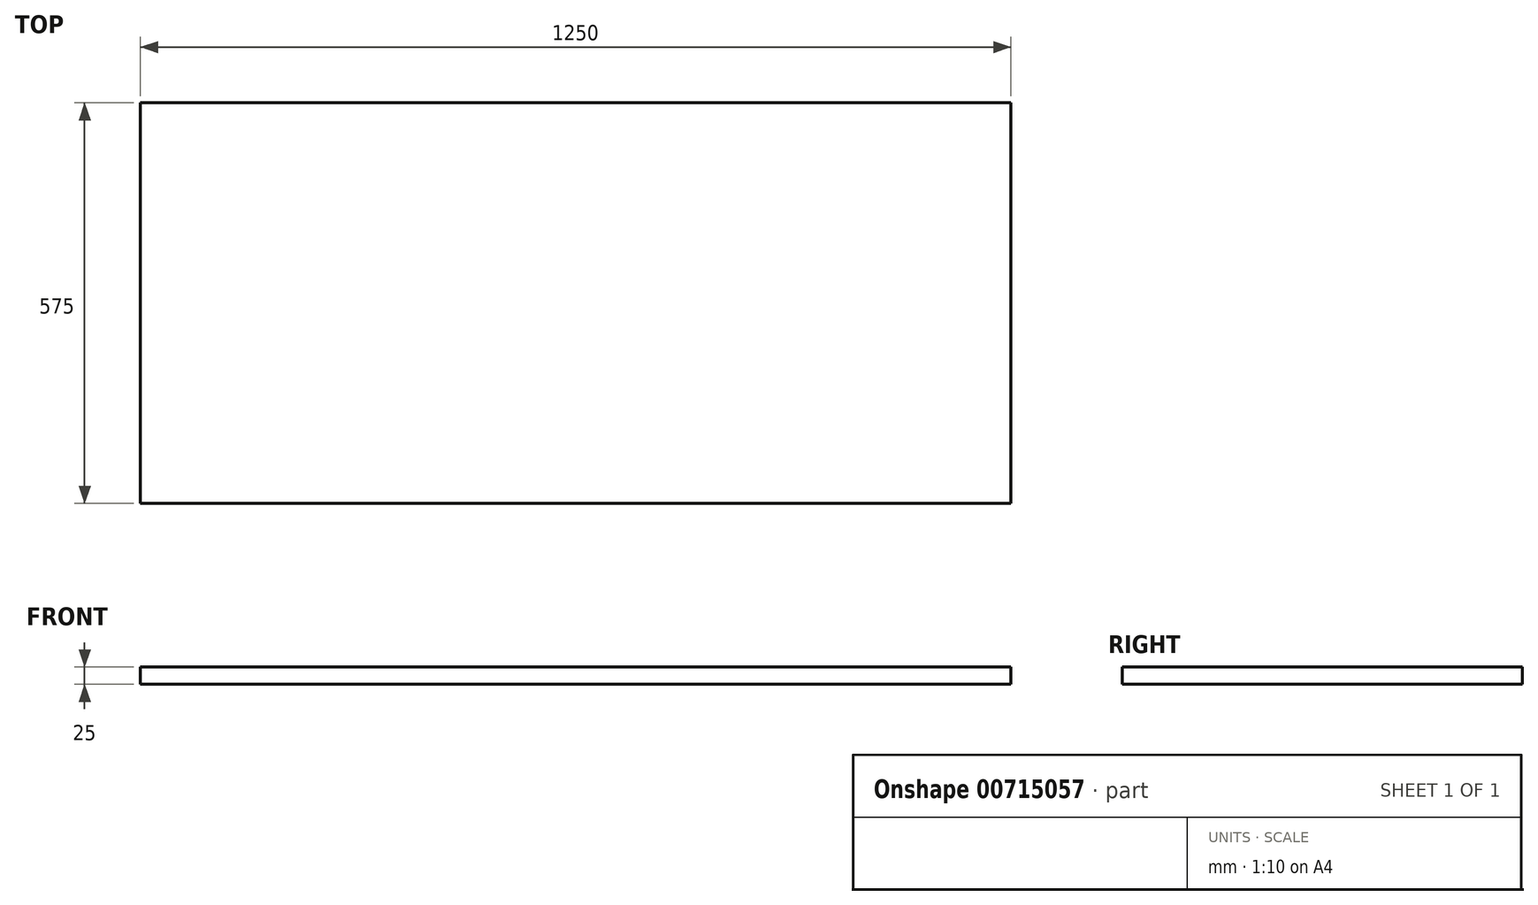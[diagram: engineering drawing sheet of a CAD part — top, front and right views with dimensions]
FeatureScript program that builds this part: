
annotation { "Feature Type Name" : "Feature", "Feature Type Description" : "" }
export const myFeature = defineFeature(function(context is Context, id is Id, definition is map)
    precondition{}
    {
        {
            var Q0;
            Q0=qCreatedBy(makeId("Top.planeOp"),FACE);
            var sketch = newSketch(context, id + "F0", { "sketchPlane" : qUnion([Q0])});
            skLineSegment(sketch, "E0.bottom", {"start": v(625, 287.5) * mm, "end": v(-625, 287.5) * mm});
            skLineSegment(sketch, "E0.top", {"start": v(625, -287.5) * mm, "end": v(-625, -287.5) * mm});
            skLineSegment(sketch, "E0.left", {"start": v(625, 287.5) * mm, "end": v(625, -287.5) * mm});
            skLineSegment(sketch, "E0.right", {"start": v(-625, 287.5) * mm, "end": v(-625, -287.5) * mm});
            skPoint(sketch, "E0.middle", {"position": v(0, 0) * mm});
            skSolve(sketch);
        }
        {
            var Q0;
            Q0=makeQuery(id+"F0.imprint","IMPRINT",FACE,{"disambiguationData":[TD([[makeQuery(id+"F0.imprint","IMPRINT",EDGE,{"derivedFrom":sQuery(id+"F0.wireOp",EDGE,"E0.bottom")}),1.0]])]});
            extrude(context, id + "F1", {"entities" : qUnion([Q0]), "depth" : 25 * mm, "offsetDistance" : 25 * mm});
        }
    });
